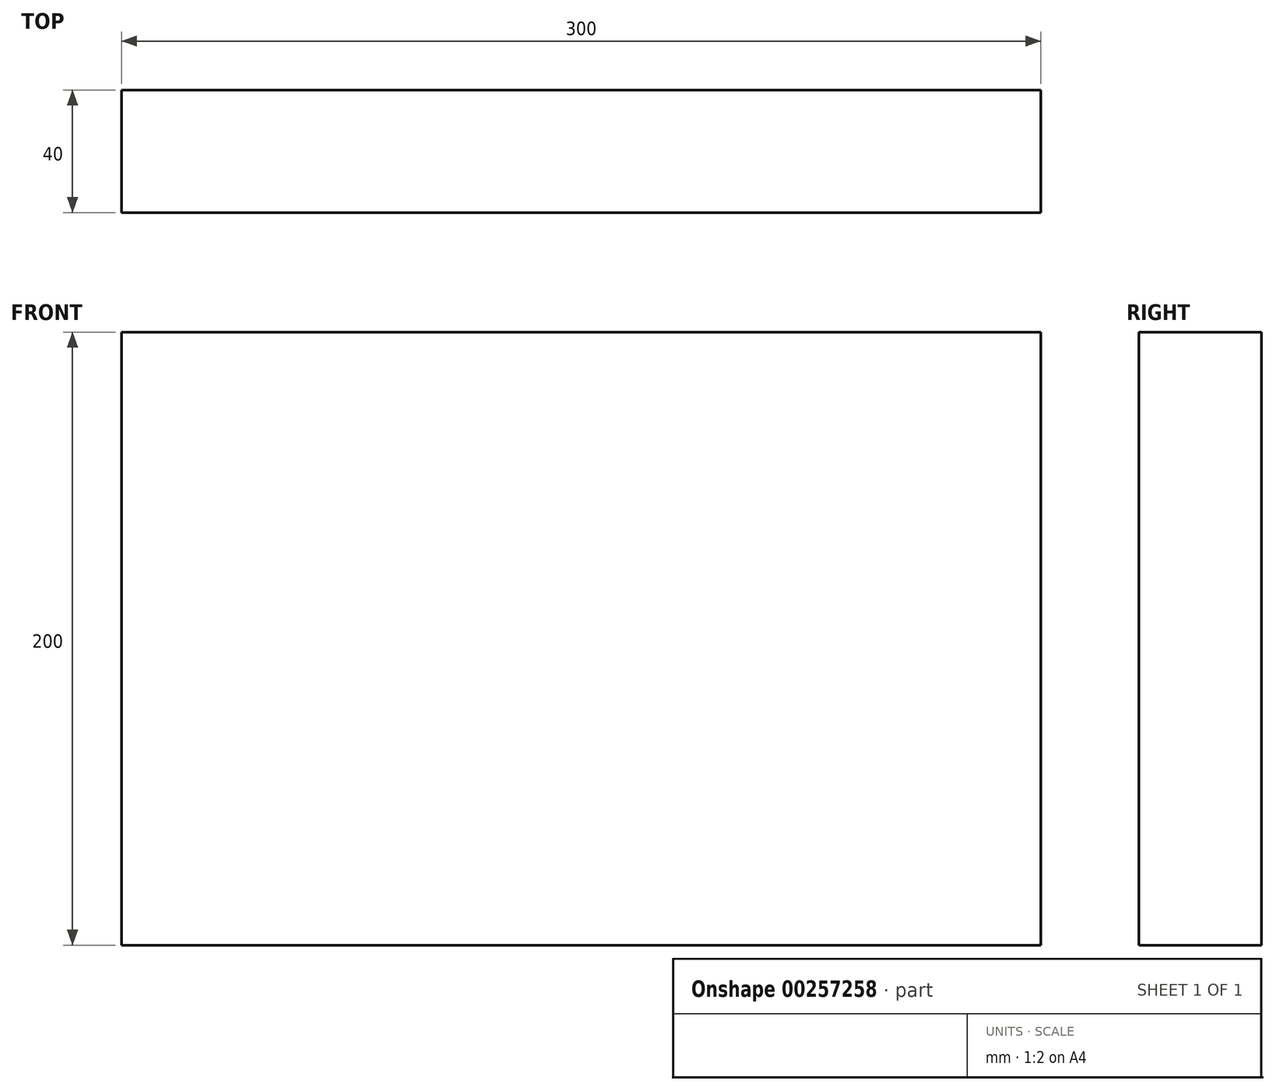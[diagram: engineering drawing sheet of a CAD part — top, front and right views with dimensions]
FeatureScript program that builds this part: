
annotation { "Feature Type Name" : "Feature", "Feature Type Description" : "" }
export const myFeature = defineFeature(function(context is Context, id is Id, definition is map)
    precondition{}
    {
        {
            var Q0;
            Q0=qCreatedBy(makeId("Front.planeOp"),FACE);
            var sketch = newSketch(context, id + "F0", { "sketchPlane" : qUnion([Q0])});
            skLineSegment(sketch, "E0.bottom", {"start": v(150, 100) * mm, "end": v(-150, 100) * mm});
            skLineSegment(sketch, "E0.top", {"start": v(150, -100) * mm, "end": v(-150, -100) * mm});
            skLineSegment(sketch, "E0.left", {"start": v(150, 100) * mm, "end": v(150, -100) * mm});
            skLineSegment(sketch, "E0.right", {"start": v(-150, 100) * mm, "end": v(-150, -100) * mm});
            skPoint(sketch, "E0.middle", {"position": v(0, 0) * mm});
            skSolve(sketch);
        }
        {
            var Q0;
            Q0=makeQuery(id+"F0.imprint","IMPRINT",FACE,{"disambiguationData":[TD([[makeQuery(id+"F0.imprint","IMPRINT",EDGE,{"derivedFrom":sQuery(id+"F0.wireOp",EDGE,"E0.bottom")}),1.0]])]});
            extrude(context, id + "F1", {"entities" : qUnion([Q0]), "depth" : 40 * mm});
        }
    });
